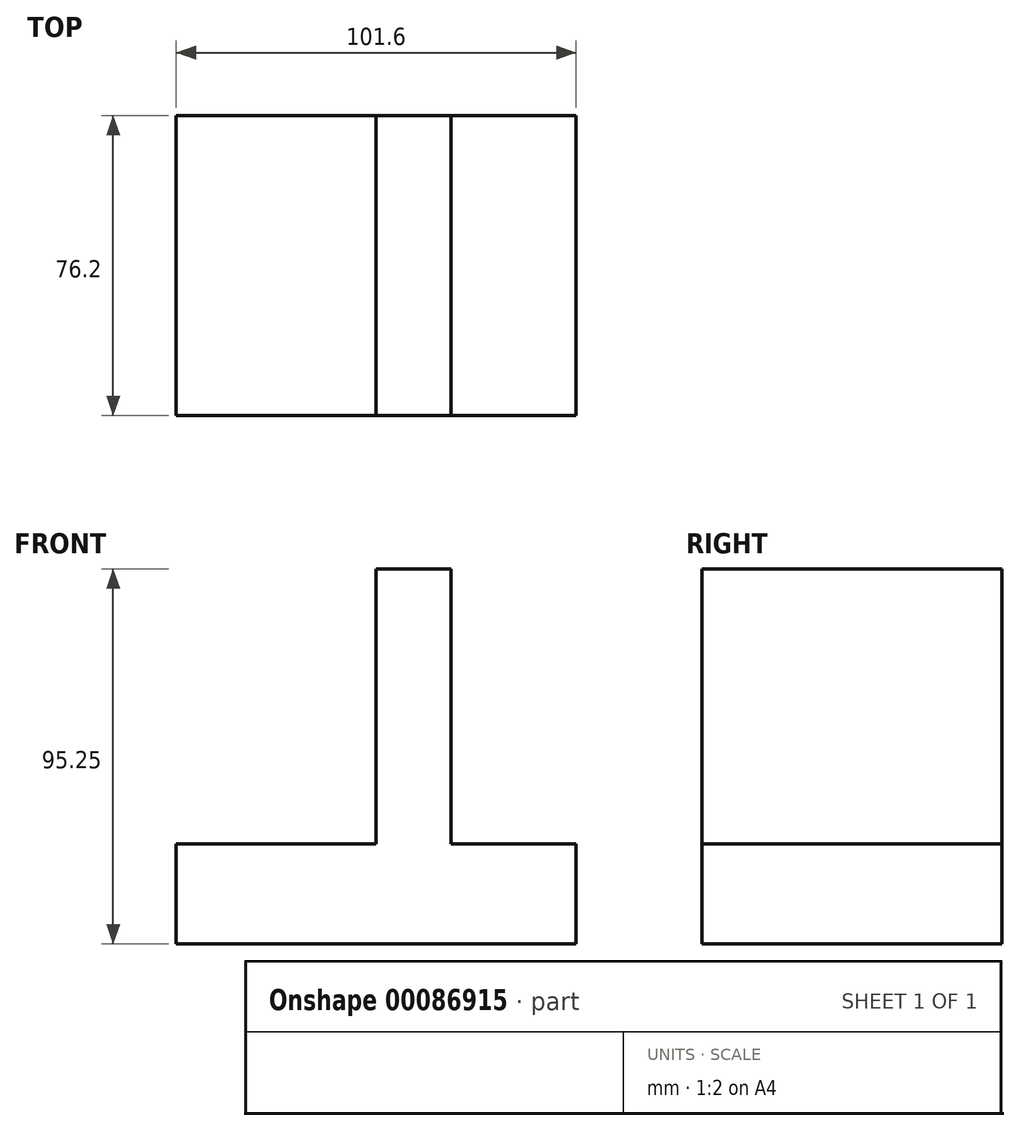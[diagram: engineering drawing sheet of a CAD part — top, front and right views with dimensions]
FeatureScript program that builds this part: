
annotation { "Feature Type Name" : "Feature", "Feature Type Description" : "" }
export const myFeature = defineFeature(function(context is Context, id is Id, definition is map)
    precondition{}
    {
        {
            var Q0;
            Q0=qCreatedBy(makeId("Top.planeOp"),FACE);
            var sketch = newSketch(context, id + "F0", { "sketchPlane" : qUnion([Q0])});
            skLineSegment(sketch, "E0.bottom", {"start": v(-60.02, -37.69) * mm, "end": v(41.58, -37.69) * mm});
            skLineSegment(sketch, "E0.top", {"start": v(-60.02, 38.51) * mm, "end": v(41.58, 38.51) * mm});
            skLineSegment(sketch, "E0.left", {"start": v(-60.02, -37.69) * mm, "end": v(-60.02, 38.51) * mm});
            skLineSegment(sketch, "E0.right", {"start": v(41.58, -37.69) * mm, "end": v(41.58, 38.51) * mm});
            skSolve(sketch);
        }
        {
            var Q0;
            Q0=makeQuery(id+"F0.imprint","IMPRINT",FACE,{"disambiguationData":[TD([[makeQuery(id+"F0.imprint","IMPRINT",EDGE,{"derivedFrom":sQuery(id+"F0.wireOp",EDGE,"E0.bottom")}),1.0]])]});
            extrude(context, id + "F1", {"entities" : qUnion([Q0]), "depth" : 95.25 * mm});
        }
        {
            var Q0;
            Q0=makeQuery(id+"F1.opExtrude","CAP_FACE",FACE,{"disambiguationData":[OSD([sQuery(id+"F0.wireOp",EDGE,"E0.bottom"),sQuery(id+"F0.wireOp",EDGE,"E0.top"),sQuery(id+"F0.wireOp",EDGE,"E0.left"),sQuery(id+"F0.wireOp",EDGE,"E0.right")])],"isStart":false});
            var sketch = newSketch(context, id + "F2", { "sketchPlane" : qUnion([Q0])});
            skLineSegment(sketch, "E1.bottom", {"start": v(-60.02, 38.51) * mm, "end": v(-9.22, 38.51) * mm});
            skLineSegment(sketch, "E1.top", {"start": v(-60.02, -37.69) * mm, "end": v(-9.22, -37.69) * mm});
            skLineSegment(sketch, "E1.left", {"start": v(-60.02, 38.51) * mm, "end": v(-60.02, -37.69) * mm});
            skLineSegment(sketch, "E1.right", {"start": v(-9.22, 38.51) * mm, "end": v(-9.22, -37.69) * mm});
            skSolve(sketch);
        }
        {
            var Q0;
            Q0=makeQuery(id+"F2.imprint","IMPRINT",FACE,{"disambiguationData":[TD([[makeQuery(id+"F2.imprint","IMPRINT",EDGE,{"derivedFrom":sQuery(id+"F2.wireOp",EDGE,"E1.bottom")}),-1.0]])]});
            extrude(context, id + "F3", {"entities" : qUnion([Q0]), "operationType" : NewBodyOperationType.REMOVE, "oppositeDirection" : true, "depth" : 69.85 * mm});
        }
        {
            var Q0;
            Q0=makeQuery(id+"F1.opExtrude","CAP_FACE",FACE,{"disambiguationData":[OSD([sQuery(id+"F0.wireOp",EDGE,"E0.bottom"),sQuery(id+"F0.wireOp",EDGE,"E0.top"),sQuery(id+"F0.wireOp",EDGE,"E0.left"),sQuery(id+"F0.wireOp",EDGE,"E0.right")])],"isStart":false});
            var sketch = newSketch(context, id + "F4", { "sketchPlane" : qUnion([Q0])});
            skLineSegment(sketch, "E2.bottom", {"start": v(41.58, 38.51) * mm, "end": v(9.83, 38.51) * mm});
            skLineSegment(sketch, "E2.top", {"start": v(41.58, -37.69) * mm, "end": v(9.83, -37.69) * mm});
            skLineSegment(sketch, "E2.left", {"start": v(41.58, 38.51) * mm, "end": v(41.58, -37.69) * mm});
            skLineSegment(sketch, "E2.right", {"start": v(9.83, 38.51) * mm, "end": v(9.83, -37.69) * mm});
            skSolve(sketch);
        }
        {
            var Q0;
            Q0=makeQuery(id+"F4.imprint","IMPRINT",FACE,{"disambiguationData":[TD([[makeQuery(id+"F4.imprint","IMPRINT",EDGE,{"derivedFrom":sQuery(id+"F4.wireOp",EDGE,"E2.bottom")}),-1.0]])]});
            extrude(context, id + "F5", {"entities" : qUnion([Q0]), "operationType" : NewBodyOperationType.REMOVE, "oppositeDirection" : true, "depth" : 69.85 * mm});
        }
    });
